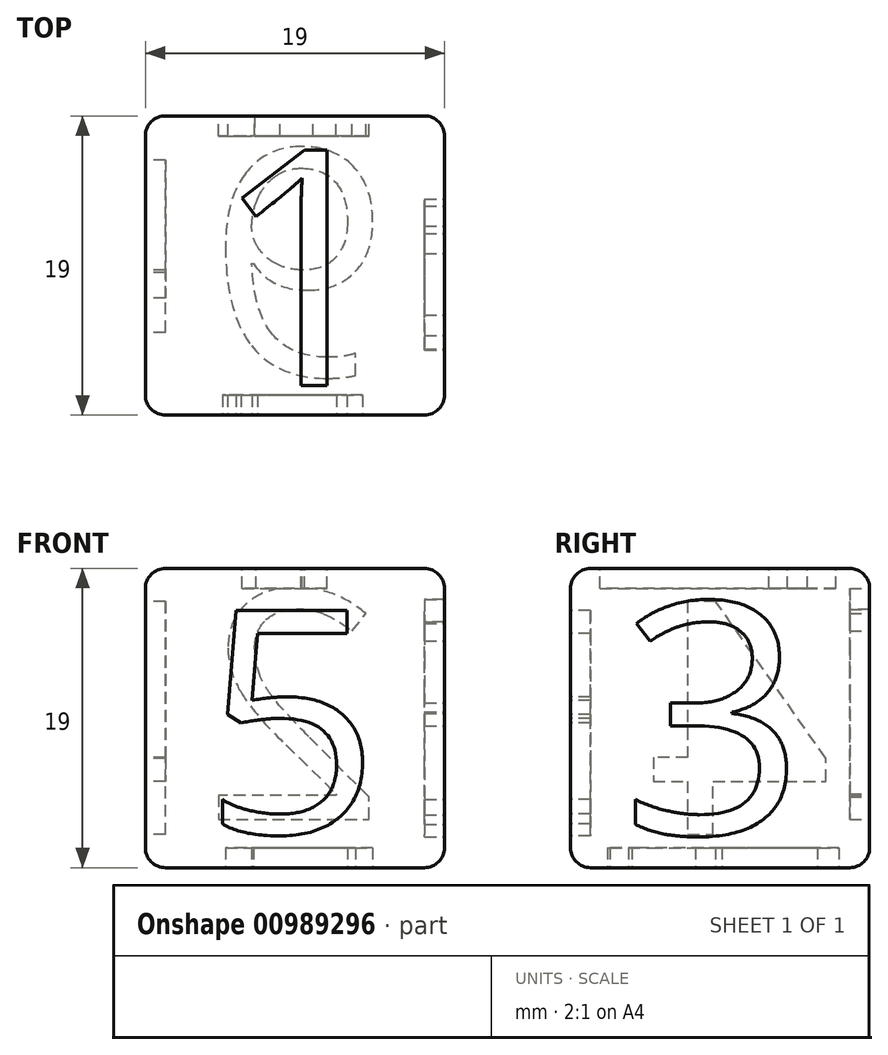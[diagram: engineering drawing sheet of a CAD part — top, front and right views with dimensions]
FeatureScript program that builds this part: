
annotation { "Feature Type Name" : "Feature", "Feature Type Description" : "" }
export const myFeature = defineFeature(function(context is Context, id is Id, definition is map)
    precondition{}
    {
        {
            var Q0;
            Q0=qCreatedBy(makeId("Top.planeOp"),FACE);
            var sketch = newSketch(context, id + "F0", { "sketchPlane" : qUnion([Q0])});
            skLineSegment(sketch, "E0.bottom", {"start": v(-8.87, 8.66) * mm, "end": v(10.13, 8.66) * mm});
            skLineSegment(sketch, "E0.top", {"start": v(-8.87, -10.34) * mm, "end": v(10.13, -10.34) * mm});
            skLineSegment(sketch, "E0.left", {"start": v(-8.87, 8.66) * mm, "end": v(-8.87, -10.34) * mm});
            skLineSegment(sketch, "E0.right", {"start": v(10.13, 8.66) * mm, "end": v(10.13, -10.34) * mm});
            skSolve(sketch);
        }
        {
            var Q0;
            Q0=makeQuery(id+"F0.imprint","IMPRINT",FACE,{"disambiguationData":[TD([[makeQuery(id+"F0.imprint","IMPRINT",EDGE,{"derivedFrom":sQuery(id+"F0.wireOp",EDGE,"E0.bottom")}),-1.0]])]});
            extrude(context, id + "F1", {"entities" : qUnion([Q0]), "depth" : 19 * mm, "offsetDistance" : 25.4 * mm});
        }
        {
            var Q0;
            Q0=makeQuery(id+"F1.opExtrude","SWEPT_EDGE",EDGE,{"disambiguationData":[OSD([sQuery(id+"F0.wireOp",EDGE,"E0.bottom"),sQuery(id+"F0.wireOp",EDGE,"E0.left")])]});
            fillet(context, id + "F2", {"entities" : qUnion([Q0]), "radius" : 1.27 * mm, "tangentPropagation" : true, "allowEdgeOverflow" : false});
        }
        {
            var Q0;
            Q0=makeQuery(id+"F1.opExtrude","CAP_EDGE",EDGE,{"disambiguationData":[OSD([sQuery(id+"F0.wireOp",EDGE,"E0.bottom")])],"isStart":false});
            fillet(context, id + "F3", {"entities" : qUnion([Q0]), "radius" : 1.27 * mm, "tangentPropagation" : true, "allowEdgeOverflow" : false});
        }
        {
            var Q0;
            Q0=makeQuery(id+"F1.opExtrude","SWEPT_EDGE",EDGE,{"disambiguationData":[OSD([sQuery(id+"F0.wireOp",EDGE,"E0.bottom"),sQuery(id+"F0.wireOp",EDGE,"E0.right")])]});
            fillet(context, id + "F4", {"entities" : qUnion([Q0]), "radius" : 1.27 * mm, "tangentPropagation" : true, "allowEdgeOverflow" : false});
        }
        {
            var Q0;
            Q0=makeQuery(id+"F1.opExtrude","CAP_EDGE",EDGE,{"disambiguationData":[OSD([sQuery(id+"F0.wireOp",EDGE,"E0.bottom")])],"isStart":true});
            fillet(context, id + "F5", {"entities" : qUnion([Q0]), "radius" : 1.27 * mm, "tangentPropagation" : true, "allowEdgeOverflow" : false});
        }
        {
            var Q0;
            Q0=makeQuery(id+"F1.opExtrude","CAP_EDGE",EDGE,{"disambiguationData":[OSD([sQuery(id+"F0.wireOp",EDGE,"E0.top")])],"isStart":false});
            fillet(context, id + "F6", {"entities" : qUnion([Q0]), "radius" : 1.27 * mm, "tangentPropagation" : true, "allowEdgeOverflow" : false});
        }
        {
            var Q0;
            Q0=makeQuery(id+"F1.opExtrude","CAP_FACE",FACE,{"disambiguationData":[OSD([sQuery(id+"F0.wireOp",EDGE,"E0.bottom"),sQuery(id+"F0.wireOp",EDGE,"E0.top"),sQuery(id+"F0.wireOp",EDGE,"E0.left"),sQuery(id+"F0.wireOp",EDGE,"E0.right")])],"isStart":false});
            var sketch = newSketch(context, id + "F7", { "sketchPlane" : qUnion([Q0])});
            skText(sketch, "E1", { "text": "1", "fontName": "OpenSans-Regular.ttf"});
            const initialGuessF7  = {"E1": [-0.00466, -0.00848, 1, 0, 0.01511]};
            skSetInitialGuess(sketch, initialGuessF7);
            skSolve(sketch);
        }
        {
            var Q0;
            Q0=makeQuery(id+"F7.imprint","IMPRINT",FACE,{"disambiguationData":[TD([[makeQuery(id+"F7.imprint","IMPRINT",EDGE,{"derivedFrom":sQuery(id+"F7.wireOp",EDGE,"E1.sketch_text.stroke-0")}),-1.0]])]});
            extrude(context, id + "F8", {"entities" : qUnion([Q0]), "operationType" : NewBodyOperationType.REMOVE, "oppositeDirection" : true, "depth" : 1.27 * mm, "offsetDistance" : 25.4 * mm});
        }
        {
            var Q0;
            Q0=makeQuery(id+"F1.opExtrude","SWEPT_FACE",FACE,{"disambiguationData":[OSD([sQuery(id+"F0.wireOp",EDGE,"E0.bottom")])]});
            var sketch = newSketch(context, id + "F9", { "sketchPlane" : qUnion([Q0])});
            skText(sketch, "E2", { "text": "2\n", "fontName": "OpenSans-Regular.ttf"});
            const initialGuessF9  = {"E2": [-0.00631, 0.00307, 1, 0, 0.01466]};
            skSetInitialGuess(sketch, initialGuessF9);
            skSolve(sketch);
        }
        {
            var Q0;
            Q0=makeQuery(id+"F1.opExtrude","SWEPT_FACE",FACE,{"disambiguationData":[OSD([sQuery(id+"F0.wireOp",EDGE,"E0.right")])]});
            var sketch = newSketch(context, id + "F10", { "sketchPlane" : qUnion([Q0])});
            skText(sketch, "E3", { "text": "3", "fontName": "OpenSans-Regular.ttf"});
            const initialGuessF10  = {"E3": [-0.00717, 0.00215, 1, 0, 0.0148]};
            skSetInitialGuess(sketch, initialGuessF10);
            skSolve(sketch);
        }
        {
            var Q0;
            Q0=makeQuery(id+"F1.opExtrude","CAP_FACE",FACE,{"disambiguationData":[OSD([sQuery(id+"F0.wireOp",EDGE,"E0.bottom"),sQuery(id+"F0.wireOp",EDGE,"E0.top"),sQuery(id+"F0.wireOp",EDGE,"E0.left"),sQuery(id+"F0.wireOp",EDGE,"E0.right")])],"isStart":true});
            var sketch = newSketch(context, id + "F11", { "sketchPlane" : qUnion([Q0])});
            skText(sketch, "E4", { "text": "6", "fontName": "OpenSans-Regular.ttf"});
            const initialGuessF11  = {"E4": [-0.00493, -0.00652, 1, 0, 0.01445]};
            skSetInitialGuess(sketch, initialGuessF11);
            skSolve(sketch);
        }
        {
            var Q0;
            Q0=makeQuery(id+"F11.imprint","IMPRINT",FACE,{"disambiguationData":[TD([[makeQuery(id+"F11.imprint","IMPRINT",EDGE,{"derivedFrom":sQuery(id+"F11.wireOp",EDGE,"E4.sketch_text.stroke-0")}),-1.0]])]});
            extrude(context, id + "F12", {"entities" : qUnion([Q0]), "operationType" : NewBodyOperationType.REMOVE, "oppositeDirection" : true, "depth" : 1.27 * mm, "offsetDistance" : 25.4 * mm});
        }
        {
            var Q0;
            Q0=makeQuery(id+"F1.opExtrude","SWEPT_FACE",FACE,{"disambiguationData":[OSD([sQuery(id+"F0.wireOp",EDGE,"E0.left")])]});
            var sketch = newSketch(context, id + "F13", { "sketchPlane" : qUnion([Q0])});
            skText(sketch, "E5", { "text": "4", "fontName": "OpenSans-Regular.ttf"});
            const initialGuessF13  = {"E5": [-0.0063, 0.0021, 1, 0, 0.01486]};
            skSetInitialGuess(sketch, initialGuessF13);
            skSolve(sketch);
        }
        {
            var Q0;
            Q0 = qSketchRegion(id + "F10", true);
            extrude(context, id + "F14", {"entities" : qUnion([Q0]), "operationType" : NewBodyOperationType.REMOVE, "oppositeDirection" : true, "depth" : 1.27 * mm, "offsetDistance" : 25.4 * mm});
        }
        {
            var Q0;
            Q0 = qSketchRegion(id + "F13", true);
            var Q1;
            Q1=makeQuery(id+"F13.imprint","IMPRINT",FACE,{"disambiguationData":[TD([[makeQuery(id+"F13.imprint","IMPRINT",EDGE,{"derivedFrom":sQuery(id+"F13.wireOp",EDGE,"E5.sketch_text.stroke-11")}),1.0]])]});
            extrude(context, id + "F15", {"entities" : qUnion([Q0, Q1]), "operationType" : NewBodyOperationType.REMOVE, "oppositeDirection" : true, "depth" : 1.27 * mm, "offsetDistance" : 25.4 * mm});
        }
        {
            var Q0;
            Q0=makeQuery(id+"F9.imprint","IMPRINT",FACE,{"disambiguationData":[TD([[makeQuery(id+"F9.imprint","IMPRINT",EDGE,{"derivedFrom":sQuery(id+"F9.wireOp",EDGE,"E2.sketch_text.stroke-0")}),-1.0]])]});
            extrude(context, id + "F16", {"entities" : qUnion([Q0]), "operationType" : NewBodyOperationType.REMOVE, "oppositeDirection" : true, "depth" : 1.27 * mm, "offsetDistance" : 25.4 * mm});
        }
        {
            var Q0;
            Q0=makeQuery(id+"F1.opExtrude","SWEPT_FACE",FACE,{"disambiguationData":[OSD([sQuery(id+"F0.wireOp",EDGE,"E0.top")])]});
            var sketch = newSketch(context, id + "F17", { "sketchPlane" : qUnion([Q0])});
            skText(sketch, "E6", { "text": "5", "fontName": "OpenSans-Regular.ttf"});
            const initialGuessF17  = {"E6": [-0.0051, 0.0021, 1, 0, 0.01481]};
            skSetInitialGuess(sketch, initialGuessF17);
            skSolve(sketch);
        }
        {
            var Q0;
            Q0=makeQuery(id+"F17.imprint","IMPRINT",FACE,{"disambiguationData":[TD([[makeQuery(id+"F17.imprint","IMPRINT",EDGE,{"derivedFrom":sQuery(id+"F17.wireOp",EDGE,"E6.sketch_text.stroke-0")}),1.0]])]});
            extrude(context, id + "F18", {"entities" : qUnion([Q0]), "operationType" : NewBodyOperationType.ADD, "oppositeDirection" : true, "depth" : 1.27 * mm, "offsetDistance" : 25.4 * mm});
        }
        {
            var Q0;
            Q0=makeQuery(id+"F1.opExtrude","SWEPT_FACE",FACE,{"disambiguationData":[OSD([sQuery(id+"F0.wireOp",EDGE,"E0.top")])]});
            var sketch = newSketch(context, id + "F19", { "sketchPlane" : qUnion([Q0])});
            skText(sketch, "E7", { "text": "5", "fontName": "OpenSans-Regular.ttf"});
            const initialGuessF19  = {"E7": [-0.00527, 0.00221, 1, 0, 0.01426]};
            skSetInitialGuess(sketch, initialGuessF19);
            skSolve(sketch);
        }
        {
            var Q0;
            Q0 = qSketchRegion(id + "F19", true);
            extrude(context, id + "F20", {"entities" : qUnion([Q0]), "operationType" : NewBodyOperationType.REMOVE, "oppositeDirection" : true, "depth" : 1.27 * mm, "offsetDistance" : 25.4 * mm});
        }
    });
